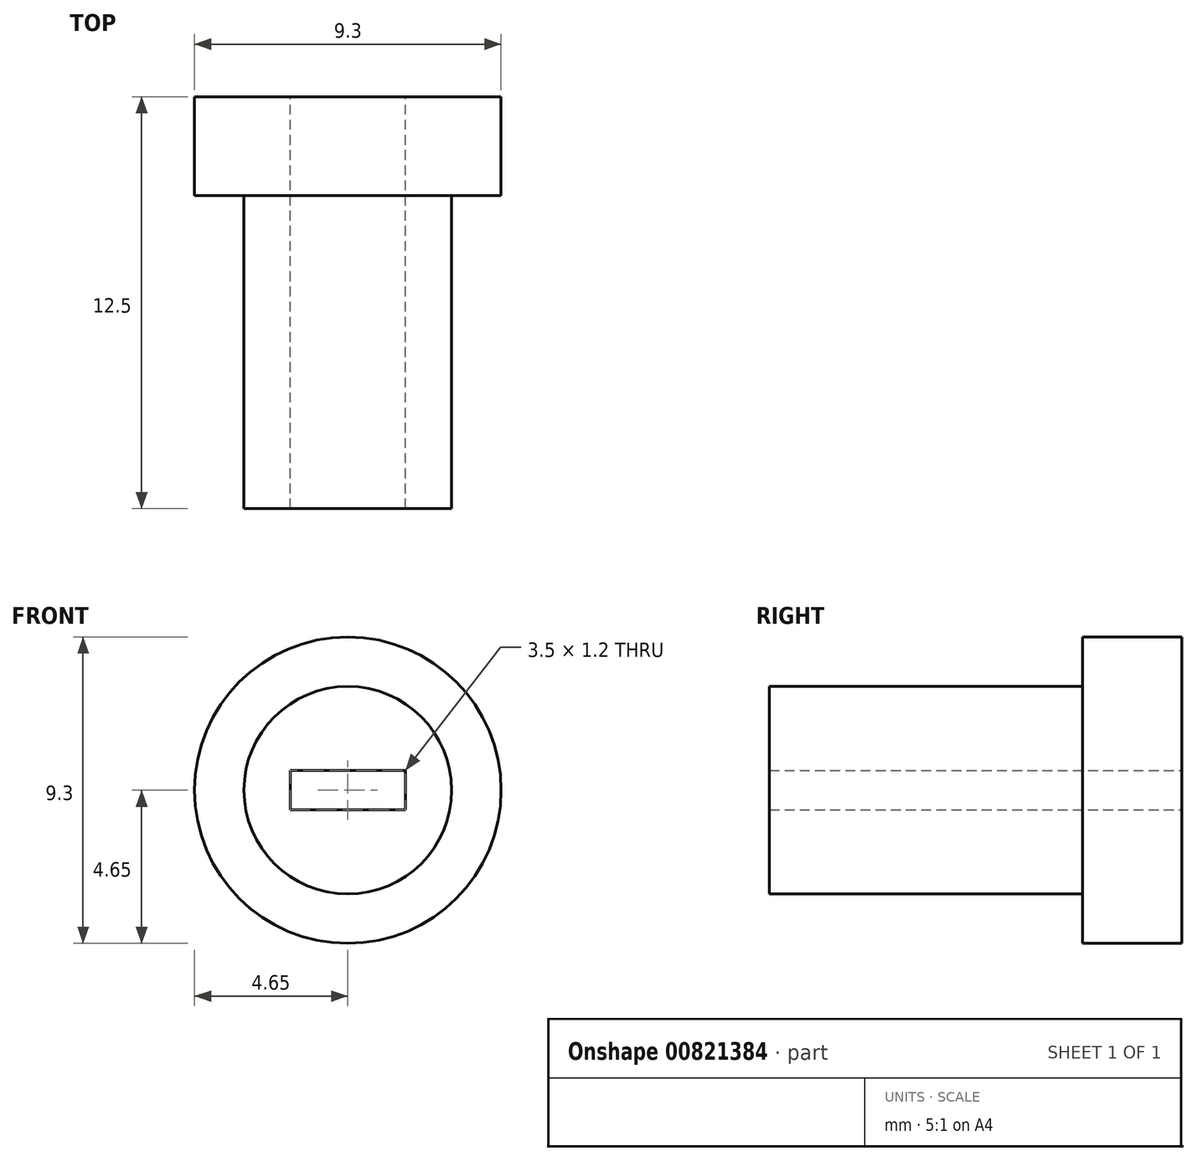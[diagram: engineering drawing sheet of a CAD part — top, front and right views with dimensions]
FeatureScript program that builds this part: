
annotation { "Feature Type Name" : "Feature", "Feature Type Description" : "" }
export const myFeature = defineFeature(function(context is Context, id is Id, definition is map)
    precondition{}
    {
        {
            var Q0;
            Q0=qCreatedBy(makeId("Front.planeOp"),FACE);
            var sketch = newSketch(context, id + "F0", { "sketchPlane" : qUnion([Q0])});
            skCircle(sketch, "E0", {"center": v(0, 0) * mm, "radius": 3.15 * mm});
            skLineSegment(sketch, "E1.bottom", {"start": v(1.75, -0.6) * mm, "end": v(-1.75, -0.6) * mm});
            skLineSegment(sketch, "E1.top", {"start": v(1.75, 0.6) * mm, "end": v(-1.75, 0.6) * mm});
            skLineSegment(sketch, "E1.left", {"start": v(1.75, -0.6) * mm, "end": v(1.75, 0.6) * mm});
            skLineSegment(sketch, "E1.right", {"start": v(-1.75, -0.6) * mm, "end": v(-1.75, 0.6) * mm});
            skCircle(sketch, "E2", {"center": v(0, 0) * mm, "radius": 4.65 * mm});
            skSolve(sketch);
        }
        {
            var Q0;
            Q0 = qSketchRegion(id + "F0", true);
            var Q1;
            Q1=makeQuery(id+"F0.imprint","IMPRINT",FACE,{"disambiguationData":[TD([[makeQuery(id+"F0.imprint","IMPRINT",EDGE,{"derivedFrom":sQuery(id+"F0.wireOp",EDGE,"E0")}),-1.0]])]});
            var Q2;
            Q2=makeQuery(id+"F0.imprint","IMPRINT",FACE,{"disambiguationData":[TD([[makeQuery(id+"F0.imprint","IMPRINT",EDGE,{"derivedFrom":sQuery(id+"F0.wireOp",EDGE,"E0")}),1.0]])]});
            extrude(context, id + "F1", {"entities" : qUnion([Q0, Q1, Q2]), "depth" : 2 * mm, "offsetDistance" : 25 * mm});
        }
        {
            var Q0;
            Q0=makeQuery(id+"F0.imprint","IMPRINT",FACE,{"disambiguationData":[TD([[makeQuery(id+"F0.imprint","IMPRINT",EDGE,{"derivedFrom":sQuery(id+"F0.wireOp",EDGE,"E0")}),-1.0]])]});
            var Q1;
            Q1=makeQuery(id+"F0.imprint","IMPRINT",FACE,{"disambiguationData":[TD([[makeQuery(id+"F0.imprint","IMPRINT",EDGE,{"derivedFrom":sQuery(id+"F0.wireOp",EDGE,"E0")}),1.0]])]});
            extrude(context, id + "F2", {"entities" : qUnion([Q0, Q1]), "operationType" : NewBodyOperationType.ADD, "depth" : 3 * mm, "offsetDistance" : 25 * mm});
        }
        {
            var Q0;
            Q0=makeQuery(id+"F0.imprint","IMPRINT",FACE,{"disambiguationData":[TD([[makeQuery(id+"F0.imprint","IMPRINT",EDGE,{"derivedFrom":sQuery(id+"F0.wireOp",EDGE,"E0")}),1.0]])]});
            extrude(context, id + "F3", {"entities" : qUnion([Q0]), "operationType" : NewBodyOperationType.ADD, "depth" : 12.5 * mm, "offsetDistance" : 25 * mm});
        }
    });
